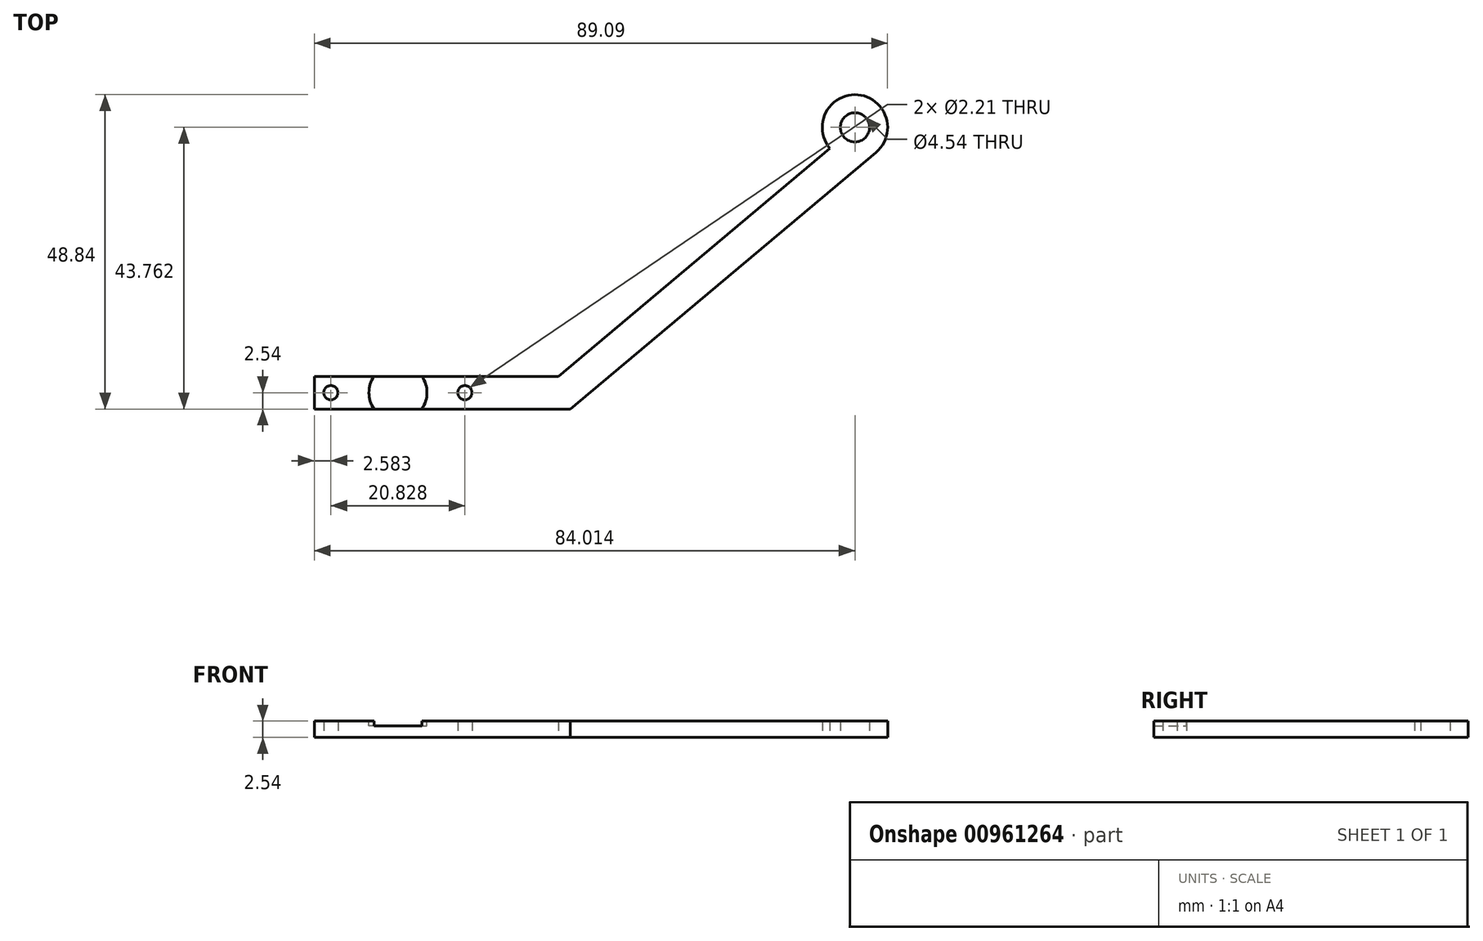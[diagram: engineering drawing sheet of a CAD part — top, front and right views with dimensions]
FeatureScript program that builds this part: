
annotation { "Feature Type Name" : "Feature", "Feature Type Description" : "" }
export const myFeature = defineFeature(function(context is Context, id is Id, definition is map)
    precondition{}
    {
        {
            var Q0;
            Q0=qCreatedBy(makeId("Top.planeOp"),FACE);
            var sketch = newSketch(context, id + "F0", { "sketchPlane" : qUnion([Q0])});
            skLineSegment(sketch, "E0", {"start": v(-4.9, 10.65) * mm, "end": v(20.03, 10.65) * mm});
            skLineSegment(sketch, "E1", {"start": v(21.87, 5.57) * mm, "end": v(-4.9, 5.57) * mm});
            skCircle(sketch, "E2", {"center": v(5.52, 8.11) * mm, "radius": 1.1 * mm});
            skLineSegment(sketch, "E3", {"start": v(-4.9, 8.11) * mm, "end": v(24.29, 8.11) * mm, "construction": true});
            skLineSegment(sketch, "E4", {"start": v(-4.9, 10.65) * mm, "end": v(-15.33, 10.65) * mm});
            skLineSegment(sketch, "E5", {"start": v(-17.89, 7.76) * mm, "end": v(-17.89, 6.92) * mm});
            skLineSegment(sketch, "E6", {"start": v(-15.22, 5.57) * mm, "end": v(-4.9, 5.57) * mm});
            skLineSegment(sketch, "E7", {"start": v(-4.9, 10.65) * mm, "end": v(-4.9, 5.57) * mm, "construction": true});
            skCircle(sketch, "E8.MirrorC", {"center": v(-15.3, 8.11) * mm, "radius": 1.1 * mm});
            skPoint(sketch, "E9.visualSharp", {"position": v(-17.89, 10.65) * mm});
            skPoint(sketch, "E10.visualSharp", {"position": v(-17.89, 5.57) * mm});
            skPoint(sketch, "E11.visualSharp", {"position": v(78.9, 10.65) * mm});
            skLineSegment(sketch, "E12", {"start": v(-15.33, 10.65) * mm, "end": v(-17.89, 10.65) * mm});
            skLineSegment(sketch, "E13", {"start": v(-17.89, 10.65) * mm, "end": v(-17.89, 7.76) * mm});
            skLineSegment(sketch, "E14", {"start": v(-17.89, 6.92) * mm, "end": v(-17.89, 5.57) * mm});
            skLineSegment(sketch, "E15", {"start": v(-17.89, 5.57) * mm, "end": v(-15.22, 5.57) * mm});
            skLineSegment(sketch, "E16", {"start": v(21.87, 5.57) * mm, "end": v(69.39, 45.44) * mm});
            skLineSegment(sketch, "E17", {"start": v(62.23, 46.07) * mm, "end": v(20.03, 10.65) * mm});
            skArc(sketch, "E18", {"start": v(69.39, 45.44) * mm, "mid": v(66.57, 54.4) * mm, "end": v(62.23, 46.07) * mm});
            skCircle(sketch, "E19", {"center": v(66.12, 49.33) * mm, "radius": 2.27 * mm});
            skSolve(sketch);
        }
        {
            var Q0;
            Q0=makeQuery(id+"F0.imprint","IMPRINT",FACE,{"disambiguationData":[TD([[makeQuery(id+"F0.imprint","IMPRINT",EDGE,{"derivedFrom":sQuery(id+"F0.wireOp",EDGE,"E0")}),-1.0]])]});
            extrude(context, id + "F1", {"entities" : qUnion([Q0]), "depth" : 2.54 * mm, "offsetDistance" : 25.4 * mm});
        }
        {
            var Q0;
            Q0=makeQuery(id+"F1.opExtrude","CAP_FACE",FACE,{"disambiguationData":[OSD([sQuery(id+"F0.wireOp",EDGE,"E0"),sQuery(id+"F0.wireOp",EDGE,"E1"),sQuery(id+"F0.wireOp",EDGE,"UvRuMUGZ-i6uX-putb-bLKE-L9GcNlpNLqzt"),sQuery(id+"F0.wireOp",EDGE,"MGwW5vhl-QvBD-U99E-h15W-jgb9tVLvbK6f"),sQuery(id+"F0.wireOp",EDGE,"E2"),sQuery(id+"F0.wireOp",EDGE,"E4"),sQuery(id+"F0.wireOp",EDGE,"E5"),sQuery(id+"F0.wireOp",EDGE,"E6"),sQuery(id+"F0.wireOp",EDGE,"E8.MirrorC"),sQuery(id+"F0.wireOp",EDGE,"bPe97rn4-rtGU-Unre-6jCB-BO6g0TyfShsA"),sQuery(id+"F0.wireOp",EDGE,"57xhoaK2-RHe5-oZaV-b60b-rte1LSozgF46"),sQuery(id+"F0.wireOp",EDGE,"E12"),sQuery(id+"F0.wireOp",EDGE,"E13"),sQuery(id+"F0.wireOp",EDGE,"E14"),sQuery(id+"F0.wireOp",EDGE,"E15")])],"isStart":false});
            var sketch = newSketch(context, id + "F2", { "sketchPlane" : qUnion([Q0])});
            skCircle(sketch, "E20", {"center": v(-4.88, 8.11) * mm, "radius": 4.5 * mm});
            skPoint(sketch, "E21.orphan", {"position": v(21.87, 5.57) * mm});
            skPoint(sketch, "E22.end.orphan", {"position": v(-31.64, 10.65) * mm});
            skLineSegment(sketch, "E23", {"start": v(-4.88, 5.57) * mm, "end": v(-4.88, 10.65) * mm, "construction": true});
            skSolve(sketch);
        }
        {
            var Q0;
            {var subQ1=makeQuery(id+"F1.opExtrude","CAP_EDGE",EDGE,{"disambiguationData":[OSD([sQuery(id+"F0.wireOp",EDGE,"E1")])],"isStart":false});var subQ3=sQuery(id+"F2.wireOp",EDGE,"E20");var subQ4=makeQuery(id+"F2.imprint","INTERSECT",VERTEX,{"derivedFrom":[subQ1,subQ3]});Q0=makeQuery(id+"F2.imprint","IMPRINT",FACE,{"disambiguationData":[TD([[makeQuery(id+"F2.imprint","IMPRINT",EDGE,{"disambiguationData":[TD([[subQ4,-1.0]])],"derivedFrom":subQ1}),-1.0]])]});}
            var Q1;
            {var subQ0=sQuery(id+"F2.wireOp",EDGE,"E20");var subQ1=makeQuery(id+"F1.opExtrude","CAP_EDGE",EDGE,{"disambiguationData":[OSD([sQuery(id+"F0.wireOp",EDGE,"E0"),sQuery(id+"F0.wireOp",EDGE,"E4"),sQuery(id+"F0.wireOp",EDGE,"E12")])],"isStart":false});var subQ2=makeQuery(id+"F2.imprint","INTERSECT",VERTEX,{"disambiguationData":[OD(0.0)],"derivedFrom":[subQ1,subQ0]});Q1=makeQuery(id+"F2.imprint","IMPRINT",FACE,{"disambiguationData":[TD([[makeQuery(id+"F2.imprint","IMPRINT",EDGE,{"disambiguationData":[TD([[subQ2,-1.0]])],"derivedFrom":subQ0}),1.0]])]});}
            extrude(context, id + "F3", {"entities" : qUnion([Q0, Q1]), "operationType" : NewBodyOperationType.REMOVE, "oppositeDirection" : true, "depth" : 0.76 * mm, "offsetDistance" : 25.4 * mm});
        }
    });
